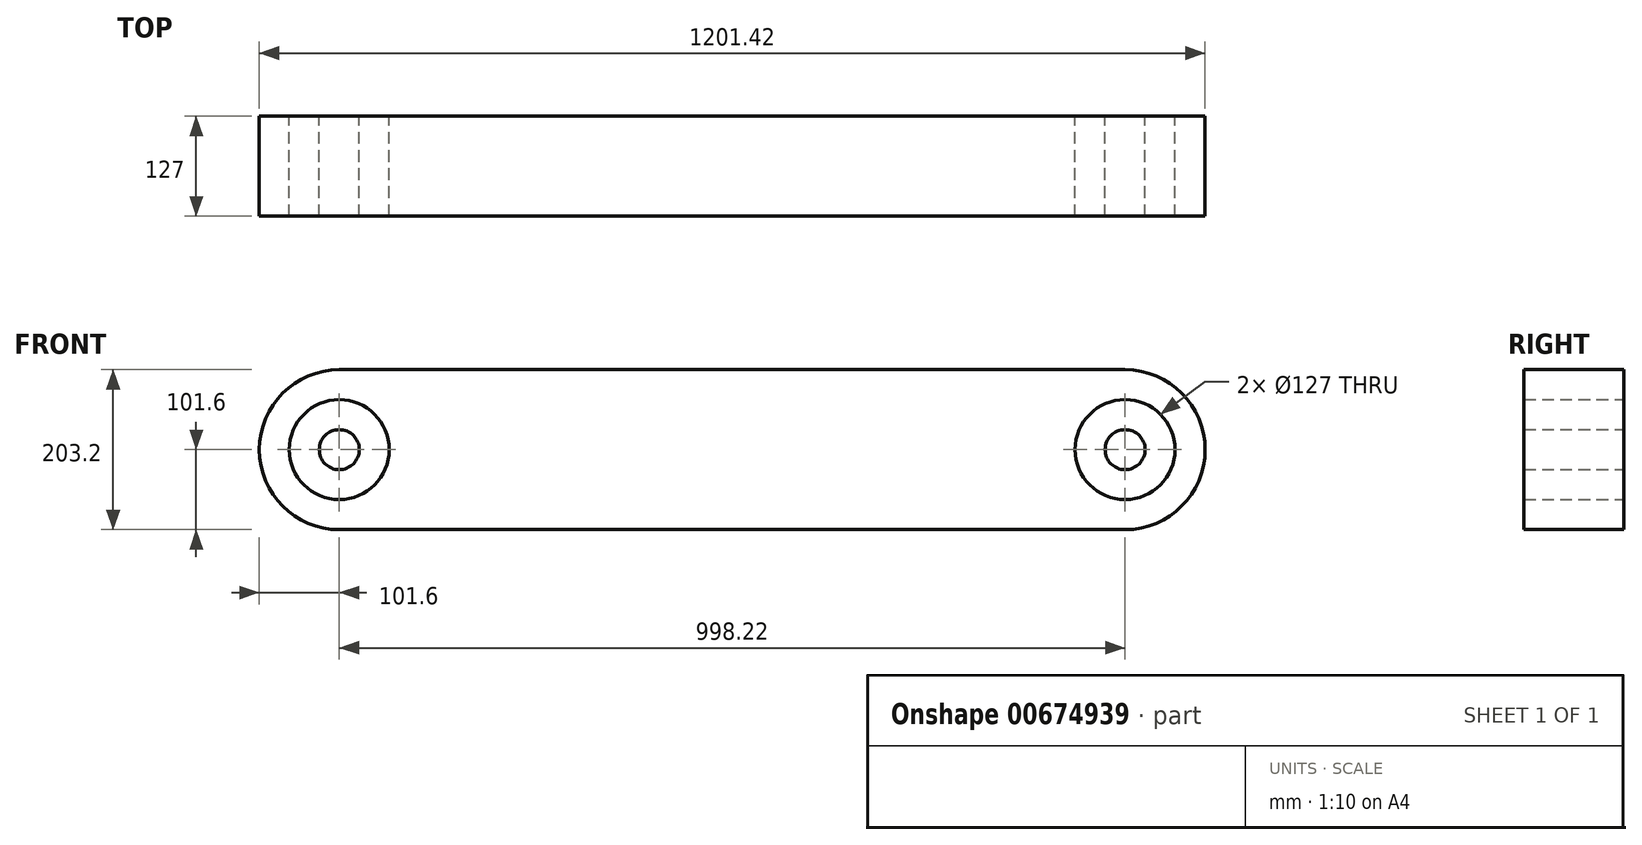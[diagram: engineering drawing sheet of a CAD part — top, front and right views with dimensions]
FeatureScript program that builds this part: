
annotation { "Feature Type Name" : "Feature", "Feature Type Description" : "" }
export const myFeature = defineFeature(function(context is Context, id is Id, definition is map)
    precondition{}
    {
        {
            var Q0;
            Q0=qCreatedBy(makeId("Front.planeOp"),FACE);
            var sketch = newSketch(context, id + "F0", { "sketchPlane" : qUnion([Q0])});
            skLineSegment(sketch, "E0.bottom", {"start": v(0, 0) * mm, "end": v(998.22, 0) * mm});
            skLineSegment(sketch, "E0.top", {"start": v(0, 203.2) * mm, "end": v(998.22, 203.2) * mm});
            skArc(sketch, "E1", {"start": v(0, 203.2) * mm, "mid": v(-101.6, 101.6) * mm, "end": v(0, 0) * mm});
            skArc(sketch, "E2", {"start": v(998.22, 0) * mm, "mid": v(1099.82, 101.6) * mm, "end": v(998.22, 203.2) * mm});
            skCircle(sketch, "E3", {"center": v(0, 101.6) * mm, "radius": 63.5 * mm});
            skCircle(sketch, "E4", {"center": v(998.22, 101.6) * mm, "radius": 63.5 * mm});
            skCircle(sketch, "E5", {"center": v(998.22, 101.6) * mm, "radius": 25.4 * mm});
            skCircle(sketch, "E6", {"center": v(0, 101.6) * mm, "radius": 25.4 * mm});
            skSolve(sketch);
        }
        {
            var Q0;
            Q0=makeQuery(id+"F0.imprint","IMPRINT",FACE,{"disambiguationData":[TD([[makeQuery(id+"F0.imprint","IMPRINT",EDGE,{"derivedFrom":sQuery(id+"F0.wireOp",EDGE,"E0.bottom")}),1.0]])]});
            var Q1;
            Q1=makeQuery(id+"F0.imprint","IMPRINT",FACE,{"disambiguationData":[TD([[makeQuery(id+"F0.imprint","IMPRINT",EDGE,{"derivedFrom":sQuery(id+"F0.wireOp",EDGE,"E6")}),1.0]])]});
            var Q2;
            Q2=makeQuery(id+"F0.imprint","IMPRINT",FACE,{"disambiguationData":[TD([[makeQuery(id+"F0.imprint","IMPRINT",EDGE,{"derivedFrom":sQuery(id+"F0.wireOp",EDGE,"E5")}),1.0]])]});
            extrude(context, id + "F1", {"entities" : qUnion([Q0, Q1, Q2]), "depth" : 127 * mm, "offsetDistance" : 25.4 * mm});
        }
    });
